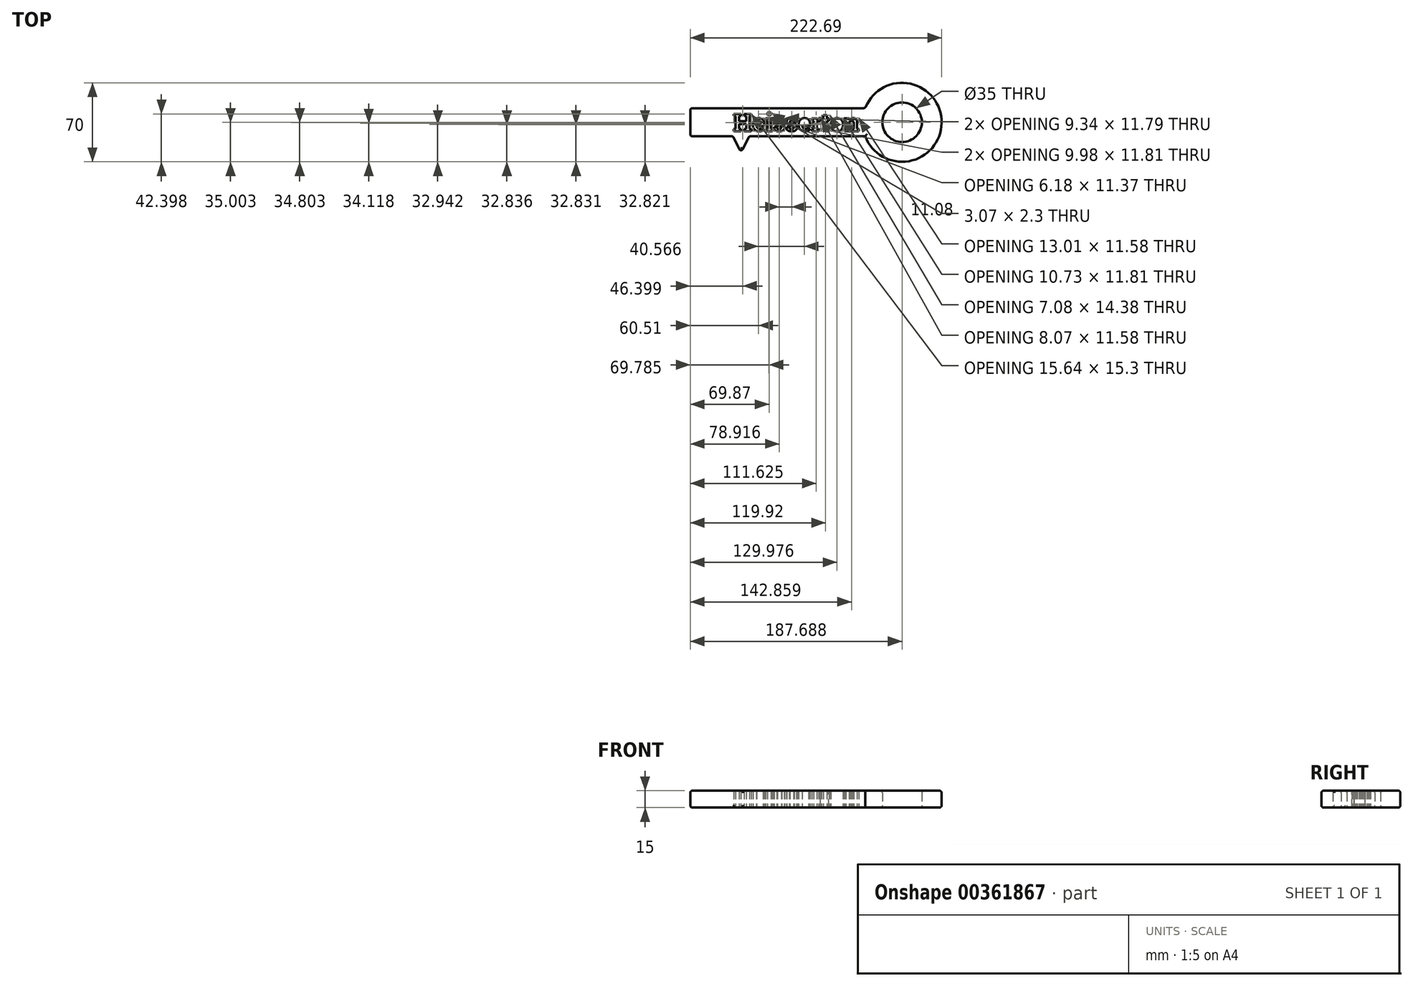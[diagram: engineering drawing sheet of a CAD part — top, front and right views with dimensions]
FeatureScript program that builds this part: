
annotation { "Feature Type Name" : "Feature", "Feature Type Description" : "" }
export const myFeature = defineFeature(function(context is Context, id is Id, definition is map)
    precondition{}
    {
        {
            var Q0;
            Q0=qCreatedBy(makeId("Top.planeOp"),FACE);
            var sketch = newSketch(context, id + "F0", { "sketchPlane" : qUnion([Q0])});
            skLineSegment(sketch, "E0.bottom", {"start": v(-61.72, 16.9) * mm, "end": v(93.28, 16.9) * mm});
            skLineSegment(sketch, "E0.top", {"start": v(-61.72, -8.1) * mm, "end": v(93.28, -8.1) * mm});
            skLineSegment(sketch, "E0.left", {"start": v(-61.72, 16.9) * mm, "end": v(-61.72, -8.1) * mm});
            skLineSegment(sketch, "E0.right", {"start": v(93.28, 16.9) * mm, "end": v(93.28, -8.1) * mm});
            skLineSegment(sketch, "E1.bottom", {"start": v(-61.72, -8.1) * mm, "end": v(-51.72, -8.1) * mm});
            skLineSegment(sketch, "E1.top", {"start": v(-61.72, -38.1) * mm, "end": v(-51.72, -38.1) * mm});
            skLineSegment(sketch, "E1.left", {"start": v(-61.72, -8.1) * mm, "end": v(-61.72, -38.1) * mm});
            skLineSegment(sketch, "E1.right", {"start": v(-51.72, -8.1) * mm, "end": v(-51.72, -38.1) * mm});
            skLineSegment(sketch, "E2.bottom", {"start": v(-41.72, -8.1) * mm, "end": v(-33.72, -8.1) * mm});
            skLineSegment(sketch, "E2.top", {"start": v(-41.72, -23.1) * mm, "end": v(-33.72, -23.1) * mm});
            skLineSegment(sketch, "E2.left", {"start": v(-41.72, -8.1) * mm, "end": v(-41.72, -23.1) * mm});
            skLineSegment(sketch, "E2.right", {"start": v(-33.72, -8.1) * mm, "end": v(-33.72, -23.1) * mm});
            skLineSegment(sketch, "E3", {"start": v(-23.72, -8.1) * mm, "end": v(-16.72, -23.1) * mm});
            skLineSegment(sketch, "E4", {"start": v(-16.72, -8.1) * mm, "end": v(-16.72, -23.1) * mm});
            skLineSegment(sketch, "E5", {"start": v(-16.72, -23.1) * mm, "end": v(-9.72, -8.1) * mm});
            skArc(sketch, "E6", {"start": v(93.28, -8.1) * mm, "mid": v(160.97, 4.4) * mm, "end": v(93.28, 16.9) * mm});
            skCircle(sketch, "E7", {"center": v(125.97, 4.4) * mm, "radius": 17.5 * mm});
            skLineSegment(sketch, "E8", {"start": v(125.97, 4.4) * mm, "end": v(-61.72, 4.4) * mm, "construction": true});
            skText(sketch, "E9", { "text": "Heisserton ", "fontName": "RobotoSlab-Bold.ttf"});
            const initialGuessF0  = {"E9": [-0.02373, -0.00346, 1, 0, 0.0155]};
            skSetInitialGuess(sketch, initialGuessF0);
            skSolve(sketch);
        }
        {
            var Q0;
            Q0=makeQuery(id+"F0.imprint","IMPRINT",FACE,{"disambiguationData":[TD([[makeQuery(id+"F0.imprint","IMPRINT",EDGE,{"derivedFrom":sQuery(id+"F0.wireOp",EDGE,"E0.bottom")}),-1.0]])]});
            var Q1;
            Q1=makeQuery(id+"F0.imprint","IMPRINT",FACE,{"disambiguationData":[TD([[makeQuery(id+"F0.imprint","IMPRINT",EDGE,{"derivedFrom":sQuery(id+"F0.wireOp",EDGE,"E1.bottom")}),-1.0]])]});
            var Q2;
            Q2=makeQuery(id+"F0.imprint","IMPRINT",FACE,{"disambiguationData":[TD([[makeQuery(id+"F0.imprint","IMPRINT",EDGE,{"derivedFrom":sQuery(id+"F0.wireOp",EDGE,"E2.bottom")}),-1.0]])]});
            var Q3;
            {var subQ0=sQuery(id+"F0.wireOp",EDGE,"E4");Q3=makeQuery(id+"F0.imprint","IMPRINT",FACE,{"disambiguationData":[TD([[makeQuery(id+"F0.imprint","IMPRINT",EDGE,{"derivedFrom":subQ0}),1.0]])]});}
            var Q4;
            {var subQ0=sQuery(id+"F0.wireOp",EDGE,"E3");Q4=makeQuery(id+"F0.imprint","IMPRINT",FACE,{"disambiguationData":[TD([[makeQuery(id+"F0.imprint","IMPRINT",EDGE,{"derivedFrom":subQ0}),1.0]])]});}
            var Q5;
            Q5=makeQuery(id+"F0.imprint","IMPRINT",FACE,{"disambiguationData":[TD([[makeQuery(id+"F0.imprint","IMPRINT",EDGE,{"derivedFrom":sQuery(id+"F0.wireOp",EDGE,"E0.right")}),1.0]])]});
            extrude(context, id + "F1", {"entities" : qUnion([Q0, Q1, Q2, Q3, Q4, Q5]), "depth" : 15 * mm});
        }
        {
            var Q0;
            Q0=makeQuery(id+"F1.opExtrude","CAP_EDGE",EDGE,{"disambiguationData":[OSD([sQuery(id+"F0.wireOp",EDGE,"E0.bottom")])],"isStart":false});
            var Q1;
            Q1=makeQuery(id+"F1.opExtrude","CAP_EDGE",EDGE,{"disambiguationData":[OSD([sQuery(id+"F0.wireOp",EDGE,"E0.left"),sQuery(id+"F0.wireOp",EDGE,"E1.left")])],"isStart":false});
            var Q2;
            Q2=makeQuery(id+"F1.opExtrude","CAP_EDGE",EDGE,{"disambiguationData":[OSD([sQuery(id+"F0.wireOp",EDGE,"E1.right")])],"isStart":false});
            var Q3;
            Q3=makeQuery(id+"F1.opExtrude","CAP_EDGE",EDGE,{"disambiguationData":[OSD([sQuery(id+"F0.wireOp",EDGE,"E1.top")])],"isStart":false});
            var Q4;
            Q4=makeQuery(id+"F1.opExtrude","CAP_EDGE",EDGE,{"disambiguationData":[OSD([sQuery(id+"F0.wireOp",EDGE,"E2.top")])],"isStart":false});
            var Q5;
            Q5=makeQuery(id+"F1.opExtrude","CAP_EDGE",EDGE,{"disambiguationData":[OSD([sQuery(id+"F0.wireOp",EDGE,"E2.right")])],"isStart":false});
            var Q6;
            Q6=makeQuery(id+"F1.opExtrude","CAP_EDGE",EDGE,{"disambiguationData":[OSD([sQuery(id+"F0.wireOp",EDGE,"E2.left")])],"isStart":false});
            var Q7;
            {var subQ0=sQuery(id+"F0.wireOp",EDGE,"E0.top");Q7=makeQuery(id+"F1.opExtrude","CAP_EDGE",EDGE,{"disambiguationData":[OSD([subQ0]),TDD([makeQuery(id+"F0.imprint","IMPRINT",EDGE,{"disambiguationData":[TD([[makeQuery(id+"F0.imprint","INTERSECT",VERTEX,{"derivedFrom":[subQ0,sQuery(id+"F0.wireOp",EDGE,"E1.bottom"),sQuery(id+"F0.wireOp",EDGE,"E1.right")]}),-1.0]])],"derivedFrom":subQ0})])],"isStart":false});}
            var Q8;
            Q8=makeQuery(id+"F1.opExtrude","CAP_EDGE",EDGE,{"disambiguationData":[OSD([sQuery(id+"F0.wireOp",EDGE,"E3")])],"isStart":false});
            var Q9;
            {var subQ0=sQuery(id+"F0.wireOp",EDGE,"E0.top");Q9=makeQuery(id+"F1.opExtrude","CAP_EDGE",EDGE,{"disambiguationData":[OSD([subQ0]),TDD([makeQuery(id+"F0.imprint","IMPRINT",EDGE,{"disambiguationData":[TD([[makeQuery(id+"F0.imprint","INTERSECT",VERTEX,{"derivedFrom":[subQ0,sQuery(id+"F0.wireOp",EDGE,"E3")]}),1.0]])],"derivedFrom":subQ0})])],"isStart":false});}
            var Q10;
            Q10=makeQuery(id+"F1.opExtrude","CAP_EDGE",EDGE,{"disambiguationData":[OSD([sQuery(id+"F0.wireOp",EDGE,"E5")])],"isStart":false});
            var Q11;
            {var subQ0=sQuery(id+"F0.wireOp",EDGE,"E0.top");Q11=makeQuery(id+"F1.opExtrude","CAP_EDGE",EDGE,{"disambiguationData":[OSD([subQ0]),TDD([makeQuery(id+"F0.imprint","IMPRINT",EDGE,{"disambiguationData":[TD([[makeQuery(id+"F0.imprint","INTERSECT",VERTEX,{"derivedFrom":[subQ0,sQuery(id+"F0.wireOp",EDGE,"E5")]}),-1.0]])],"derivedFrom":subQ0})])],"isStart":false});}
            var Q12;
            Q12=makeQuery(id+"F1.opExtrude","CAP_EDGE",EDGE,{"disambiguationData":[OSD([sQuery(id+"F0.wireOp",EDGE,"E6")])],"isStart":false});
            var Q13;
            Q13=makeQuery(id+"F1.opExtrude","CAP_EDGE",EDGE,{"disambiguationData":[OSD([sQuery(id+"F0.wireOp",EDGE,"E7")])],"isStart":false});
            var Q14;
            Q14=makeQuery(id+"F1.opExtrude","SWEPT_EDGE",EDGE,{"disambiguationData":[OSD([sQuery(id+"F0.wireOp",EDGE,"E0.bottom"),sQuery(id+"F0.wireOp",EDGE,"E0.left")])]});
            var Q15;
            Q15=makeQuery(id+"F1.opExtrude","SWEPT_EDGE",EDGE,{"disambiguationData":[OSD([sQuery(id+"F0.wireOp",EDGE,"E1.top"),sQuery(id+"F0.wireOp",EDGE,"E1.left")])]});
            var Q16;
            Q16=makeQuery(id+"F1.opExtrude","CAP_EDGE",EDGE,{"disambiguationData":[OSD([sQuery(id+"F0.wireOp",EDGE,"E6")])],"isStart":true});
            var Q17;
            Q17=makeQuery(id+"F1.opExtrude","SWEPT_FACE",FACE,{"disambiguationData":[OSD([sQuery(id+"F0.wireOp",EDGE,"E0.bottom")])]});
            var Q18;
            Q18=makeQuery(id+"F1.opExtrude","CAP_EDGE",EDGE,{"disambiguationData":[OSD([sQuery(id+"F0.wireOp",EDGE,"E0.left"),sQuery(id+"F0.wireOp",EDGE,"E1.left")])],"isStart":true});
            var Q19;
            Q19=makeQuery(id+"F1.opExtrude","CAP_EDGE",EDGE,{"disambiguationData":[OSD([sQuery(id+"F0.wireOp",EDGE,"E2.top")])],"isStart":true});
            var Q20;
            Q20=makeQuery(id+"F1.opExtrude","CAP_EDGE",EDGE,{"disambiguationData":[OSD([sQuery(id+"F0.wireOp",EDGE,"E2.right")])],"isStart":true});
            var Q21;
            Q21=makeQuery(id+"F1.opExtrude","CAP_EDGE",EDGE,{"disambiguationData":[OSD([sQuery(id+"F0.wireOp",EDGE,"E2.left")])],"isStart":true});
            var Q22;
            Q22=makeQuery(id+"F1.opExtrude","CAP_EDGE",EDGE,{"disambiguationData":[OSD([sQuery(id+"F0.wireOp",EDGE,"E1.right")])],"isStart":true});
            var Q23;
            Q23=makeQuery(id+"F1.opExtrude","CAP_EDGE",EDGE,{"disambiguationData":[OSD([sQuery(id+"F0.wireOp",EDGE,"E1.top")])],"isStart":true});
            var Q24;
            Q24=makeQuery(id+"F1.opExtrude","SWEPT_EDGE",EDGE,{"disambiguationData":[OSD([sQuery(id+"F0.wireOp",EDGE,"E1.top"),sQuery(id+"F0.wireOp",EDGE,"E1.right")])]});
            var Q25;
            Q25=makeQuery(id+"F1.opExtrude","CAP_EDGE",EDGE,{"disambiguationData":[OSD([sQuery(id+"F0.wireOp",EDGE,"E5")])],"isStart":true});
            var Q26;
            Q26=makeQuery(id+"F1.opExtrude","SWEPT_EDGE",EDGE,{"disambiguationData":[OSD([sQuery(id+"F0.wireOp",EDGE,"E3"),sQuery(id+"F0.wireOp",EDGE,"E4"),sQuery(id+"F0.wireOp",EDGE,"E5")])]});
            var Q27;
            Q27=makeQuery(id+"F1.opExtrude","SWEPT_EDGE",EDGE,{"disambiguationData":[OSD([sQuery(id+"F0.wireOp",EDGE,"E0.top"),sQuery(id+"F0.wireOp",EDGE,"E3")])]});
            var Q28;
            Q28=makeQuery(id+"F1.opExtrude","SWEPT_EDGE",EDGE,{"disambiguationData":[OSD([sQuery(id+"F0.wireOp",EDGE,"E0.top"),sQuery(id+"F0.wireOp",EDGE,"E2.bottom"),sQuery(id+"F0.wireOp",EDGE,"E2.left")])]});
            var Q29;
            {var subQ0=sQuery(id+"F0.wireOp",EDGE,"E0.top");Q29=makeQuery(id+"F1.opExtrude","CAP_EDGE",EDGE,{"disambiguationData":[OSD([subQ0]),TDD([makeQuery(id+"F0.imprint","IMPRINT",EDGE,{"disambiguationData":[TD([[makeQuery(id+"F0.imprint","INTERSECT",VERTEX,{"derivedFrom":[subQ0,sQuery(id+"F0.wireOp",EDGE,"E5")]}),-1.0]])],"derivedFrom":subQ0})])],"isStart":true});}
            var Q30;
            Q30=makeQuery(id+"F1.opExtrude","CAP_EDGE",EDGE,{"disambiguationData":[OSD([sQuery(id+"F0.wireOp",EDGE,"E7")])],"isStart":true});
            var Q31;
            {var subQ0=sQuery(id+"F0.wireOp",EDGE,"E0.top");Q31=makeQuery(id+"F1.opExtrude","CAP_EDGE",EDGE,{"disambiguationData":[OSD([subQ0]),TDD([makeQuery(id+"F0.imprint","IMPRINT",EDGE,{"disambiguationData":[TD([[makeQuery(id+"F0.imprint","INTERSECT",VERTEX,{"derivedFrom":[subQ0,sQuery(id+"F0.wireOp",EDGE,"E3")]}),1.0]])],"derivedFrom":subQ0})])],"isStart":true});}
            var Q32;
            Q32=makeQuery(id+"F1.opExtrude","SWEPT_EDGE",EDGE,{"disambiguationData":[OSD([sQuery(id+"F0.wireOp",EDGE,"E0.top"),sQuery(id+"F0.wireOp",EDGE,"E5")])]});
            var Q33;
            Q33=makeQuery(id+"F1.opExtrude","SWEPT_EDGE",EDGE,{"disambiguationData":[OSD([sQuery(id+"F0.wireOp",EDGE,"E2.top"),sQuery(id+"F0.wireOp",EDGE,"E2.right")])]});
            var Q34;
            Q34=makeQuery(id+"F1.opExtrude","SWEPT_EDGE",EDGE,{"disambiguationData":[OSD([sQuery(id+"F0.wireOp",EDGE,"E0.top"),sQuery(id+"F0.wireOp",EDGE,"E1.bottom"),sQuery(id+"F0.wireOp",EDGE,"E1.right")])]});
            fillet(context, id + "F2", {"entities" : qUnion([Q0, Q1, Q2, Q3, Q4, Q5, Q6, Q7, Q8, Q9, Q10, Q11, Q12, Q13, Q14, Q15, Q16, Q17, Q18, Q19, Q20, Q21, Q22, Q23, Q24, Q25, Q26, Q27, Q28, Q29, Q30, Q31, Q32, Q33, Q34]), "radius" : 2 * mm, "tangentPropagation" : true, "allowEdgeOverflow" : false});
        }
    });
